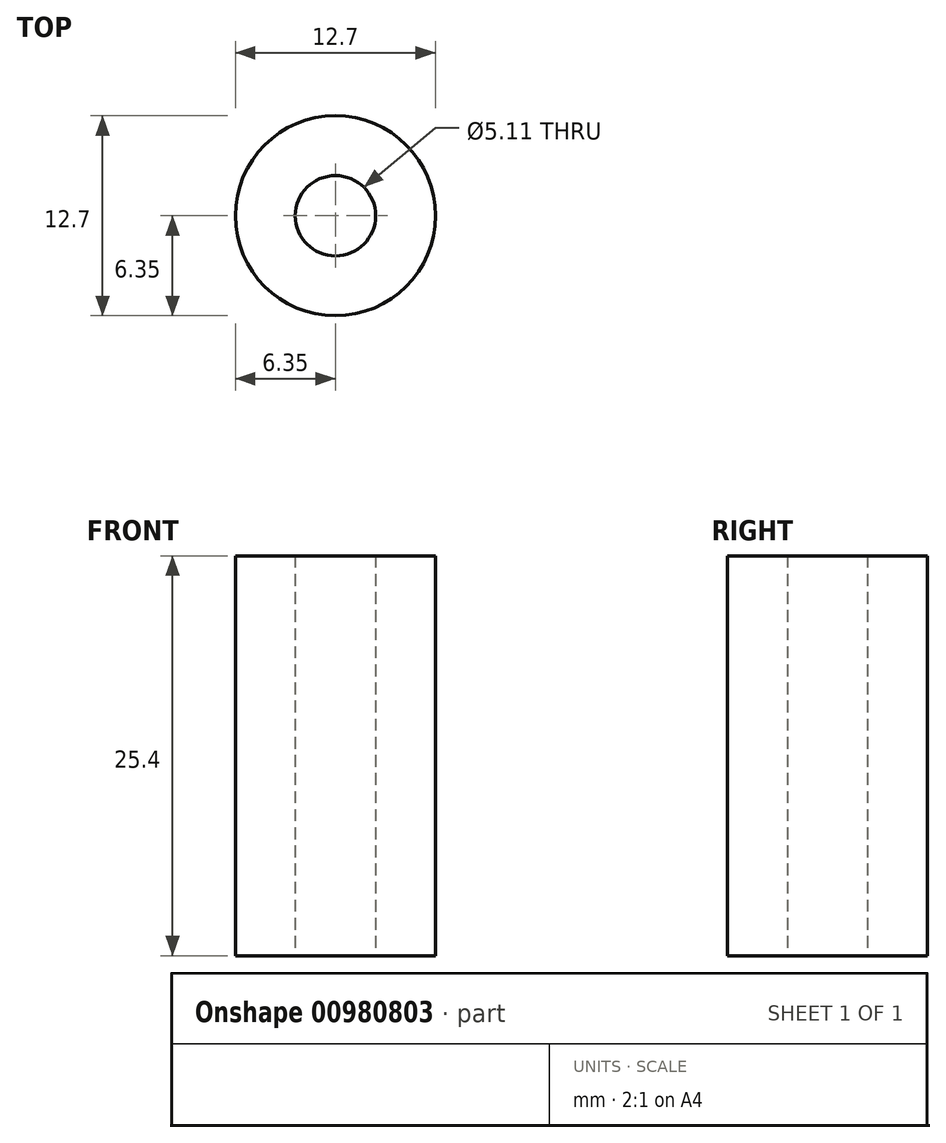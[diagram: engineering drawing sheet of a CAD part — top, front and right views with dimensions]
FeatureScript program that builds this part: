
annotation { "Feature Type Name" : "Feature", "Feature Type Description" : "" }
export const myFeature = defineFeature(function(context is Context, id is Id, definition is map)
    precondition{}
    {
        {
            var Q0;
            Q0=qCreatedBy(makeId("Top.planeOp"),FACE);
            var sketch = newSketch(context, id + "F0", { "sketchPlane" : qUnion([Q0])});
            skCircle(sketch, "E0", {"center": v(0, 0) * mm, "radius": 2.55 * mm});
            skCircle(sketch, "E1", {"center": v(0, 0) * mm, "radius": 6.35 * mm});
            skSolve(sketch);
        }
        {
            var Q0;
            Q0=qSketchRegion(id+"F0",true);
            extrude(context, id + "F1", {"entities" : qUnion([Q0]), "depth" : 25.4 * mm, "offsetDistance" : 25.4 * mm});
        }
    });
